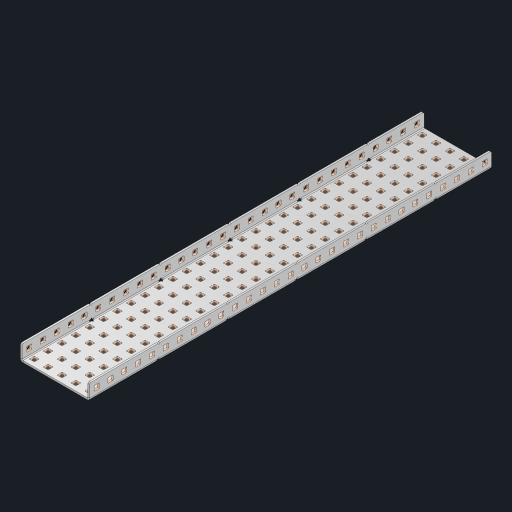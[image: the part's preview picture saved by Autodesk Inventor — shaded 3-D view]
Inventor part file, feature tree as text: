
AUTODESK INVENTOR PART (.ipt)
format: ipt  version: 2023 (Build 270158000, 158)  size: 2,219,520 bytes
history: native  units: in
note: dims shown in document units (in); Inventor stores cm internally (conversion verified against a paired STEP export)
features: other x208, extrude x202, sheet_metal_op x10, sketch x8, mirror x1, pattern_linear x1, chamfer x1
ambient origin geometry x8: Origin, YZ Plane, XZ Plane, XY Plane, X Axis, Y Axis, Z Axis, Center Point
bodies: Solid1 (feature_tree), Body (feature_tree)
feature tree (431):
  other  "Flange Pattern Plane"
  sheet_metal_op  "Flange Pattern"
  sheet_metal_op  "Body Pattern"
  other  "Arc Length"
  mirror  "Notch Mirror"
  pattern_linear  "Notch Pattern"  Spacing1=0.25in  [1 undecoded]
  chamfer  "End Chamfer"
  extrude  "Half Cut"  Depth=0.0625in
  sketch  "Sketch1"  dims[d0=2.5in]
  other  "Plate1"
  sketch  "Sketch2"  dims[d1=14.5in]
  other  "Plate2"
  sheet_metal_op  "Bend1"
  sheet_metal_op  "Corner1"
  sketch  "Sketch3"  dims[d2=0.0625in]
  other  "Flange Pattern Sketch"
  sketch  "Sketch7"  dims[d3=0.0625in]
  other  "Srf1"
  other  "Srf2"
  sketch  "Sketch8"  dims[d4=0.0312in]
  sketch  "Sketch9"  dims[d5=0.125in]
  other  "Srf91"
  sheet_metal_op  "Body Pattern Sketch"
  other  "Srf92"
  sketch  "Sketch13"  dims[d6=0.0625in]
  sketch  "Sketch14"  dims[d7=0.5in d8=90.0deg d9=0.0312in d10=0.25in d11=0.0625in d12=0.0625in d16=0.182in d17=0.02in d18=0.0625in d19=0.0in d20=0.25in d21=0.25in d46=0.172in d47=1.0in d48=0.0in d49=0.182in d50=0.02in d51=0.25in d52=0.25in d53=0.0625in d54=0.0in d55=0.172in d56=1.0in d57=0.0in d60=11.4173in d62=0.5in d63=1.9685in d65=0.5in d85=0.1473in d86=0.1782in d88=0.04in d89=0.0625in d90=0.0in d91=0.04in d92=0.0491in d95=2.5in d96=0.04in d97=0.25in d98=45.0deg d101=0.0in d102=2.497in d131=2.5in d132=11.4173in d134=0.5in d139=0.5in]
  other  "Srf856"
  other  "Srf1310"
  other  "Srf1311"
  other  "Srf1312"
  other  "Srf1376"
  other  "Srf1377"
  other  "Srf1728"
  other  "Srf1755"
  other  "Srf1878"
  other  "Srf1879"
  other  "Srf1880"
  other  "Srf1881"
  other  "Srf1882"
  other  "Srf1883"
  other  "Srf1884"
  other  "Srf1885"
  other  "Srf1886"
  other  "Srf1887"
  other  "Srf1888"
  other  "Srf1889"
  other  "Srf1890"
  other  "Srf1891"
  other  "Srf1892"
  other  "Srf1893"
  other  "Srf1894"
  other  "Srf1895"
  other  "Srf1896"
  other  "Srf1897"
  other  "Srf1898"
  other  "Srf1899"
  other  "Srf1900"
  other  "Srf1901"
  other  "Srf1902"
  other  "Srf1903"
  other  "Srf1904"
  other  "Srf1905"
  other  "Srf1906"
  other  "Srf1942"
  other  "Srf1943"
  other  "Srf1944"
  other  "Srf1945"
  other  "Srf1946"
  other  "Srf1947"
  other  "Srf1948"
  other  "Srf1949"
  other  "Srf1950"
  other  "Srf1951"
  other  "Srf1952"
  other  "Srf1953"
  other  "Srf1954"
  other  "Srf1955"
  other  "Srf1956"
  other  "Srf1957"
  other  "Srf1958"
  other  "Srf1959"
  other  "Srf1960"
  other  "Srf1961"
  other  "Srf1962"
  other  "Srf1963"
  other  "Srf1964"
  other  "Srf1965"
  other  "Srf1966"
  other  "Srf1967"
  other  "Srf1968"
  other  "Srf1969"
  other  "Srf1970"
  other  "Srf2111"
  other  "Srf2112"
  other  "Srf2113"
  other  "Srf2114"
  other  "Srf2115"
  other  "Srf2116"
  other  "Srf2117"
  other  "Srf2118"
  other  "Srf2119"
  other  "Srf2120"
  other  "Srf2121"
  other  "Srf2122"
  other  "Srf2123"
  other  "Srf2124"
  other  "Srf2125"
  other  "Srf2126"
  other  "Srf2127"
  other  "Srf2128"
  other  "Srf2129"
  other  "Srf2130"
  other  "Srf2131"
  other  "Srf2132"
  other  "Srf2133"
  other  "Srf2146"
  other  "Srf2147"
  other  "Srf2148"
  other  "Srf2149"
  other  "Srf2150"
  other  "Srf2151"
  other  "Srf2152"
  other  "Srf2153"
  other  "Srf2154"
  other  "Srf2155"
  other  "Srf2156"
  other  "Srf2157"
  other  "Srf2158"
  other  "Srf2159"
  other  "Srf2160"
  other  "Srf2161"
  other  "Srf2162"
  other  "Srf2163"
  other  "Srf2164"
  other  "Srf2165"
  other  "Srf2166"
  other  "Srf2167"
  other  "Srf2168"
  other  "Srf2169"
  other  "Srf2170"
  other  "Srf2171"
  other  "Srf2172"
  other  "Srf2173"
  other  "Srf2174"
  other  "Srf2175"
  other  "Srf2176"
  other  "Srf2177"
  other  "Srf2178"
  other  "Srf2179"
  other  "Srf2180"
  other  "Srf2181"
  other  "Srf2182"
  other  "Srf2183"
  other  "Srf2184"
  other  "Srf2185"
  other  "Srf2186"
  other  "Srf2187"
  other  "Srf2188"
  other  "Srf2189"
  other  "Srf2190"
  other  "Srf2191"
  other  "Srf2192"
  other  "Srf2193"
  other  "Srf2194"
  other  "Srf2195"
  other  "Srf2196"
  other  "Srf2197"
  other  "Srf2198"
  other  "Srf2199"
  other  "Srf2200"
  other  "Srf2201"
  other  "Srf2202"
  other  "Srf2203"
  other  "Srf2204"
  other  "Srf2205"
  other  "Srf2206"
  other  "Srf2207"
  other  "Srf2208"
  other  "Srf2209"
  other  "Srf2210"
  other  "Srf2211"
  other  "Srf2212"
  other  "Srf2213"
  other  "Srf2214"
  other  "Srf2215"
  other  "Srf2216"
  other  "Srf2217"
  other  "Srf2218"
  other  "Srf2219"
  other  "Srf2220"
  other  "Srf2221"
  other  "Srf2222"
  other  "Srf2223"
  other  "Srf2224"
  other  "Srf2225"
  other  "Srf2226"
  other  "Srf2227"
  other  "Srf2228"
  other  "Srf2229"
  other  "Srf2230"
  other  "Srf2231"
  other  "Srf2232"
  other  "Srf2233"
  other  "Srf2234"
  other  "Srf2235"
  other  "Srf2236"
  other  "Srf2237"
  other  "Srf2238"
  other  "Srf2239"
  other  "Srf2240"
  other  "Srf2241"
  other  "Srf2242"
  other  "Srf2243"
  other  "Srf2244"
  other  "Srf2245"
  other  "Srf2246"
  other  "Srf2247"
  other  "Srf2248"
  other  "Srf2249"
  other  "Srf2250"
  other  "Srf2251"
  other  "Srf2252"
  other  "Srf2253"
  other  "Srf2254"
  other  "Srf2255"
  sheet_metal_op  "Flange Stamp"
  sheet_metal_op  "Flange Circle"
  sheet_metal_op  "Body Stamp"
  sheet_metal_op  "Body Circle"
  sheet_metal_op  "Notch"
  extrude  "ExtrusionSrf2"  Depth=0.0625in
  extrude  "ExtrusionSrf92"  Depth=2.5in
  extrude  "ExtrusionSrf856"  Depth=0.02in
  extrude  "ExtrusionSrf1310"  Depth=0.0625in
  extrude  "ExtrusionSrf1311"  TaperAngle=0.0deg  [1 undecoded]
  extrude  "ExtrusionSrf1312"  Depth=0.25in
  extrude  "ExtrusionSrf1376"  Depth=0.25in
  extrude  "ExtrusionSrf1377"  Depth=2.5in
  extrude  "ExtrusionSrf1728"  Depth=2.5in TaperAngle=0.0deg
  extrude  "ExtrusionSrf1755"  Depth=2.5in
  extrude  "ExtrusionSrf1878"  Depth=0.02in
  extrude  "ExtrusionSrf1879"  Depth=0.25in
  extrude  "ExtrusionSrf1880"  Depth=0.25in
  extrude  "ExtrusionSrf1881"  Depth=0.0625in
  extrude  "ExtrusionSrf1882"  TaperAngle=0.0deg  [1 undecoded]
  extrude  "ExtrusionSrf1883"  Depth=2.5in
  extrude  "ExtrusionSrf1884"  Depth=2.5in TaperAngle=0.0deg
  extrude  "ExtrusionSrf1885"  Depth=2.5in
  extrude  "ExtrusionSrf1886"  Depth=2.5in
  extrude  "ExtrusionSrf1887"  Depth=2.5in
  extrude  "ExtrusionSrf1888"  Depth=2.5in
  extrude  "ExtrusionSrf1889"  Depth=2.5in
  extrude  "ExtrusionSrf1890"  Depth=0.0625in
  extrude  "ExtrusionSrf1891"  TaperAngle=0.0deg  [1 undecoded]
  extrude  "ExtrusionSrf1892"  Depth=2.5in
  extrude  "ExtrusionSrf1893"  Depth=2.5in
  extrude  "ExtrusionSrf1894"  Depth=2.5in
  extrude  "ExtrusionSrf1895"  Depth=0.25in TaperAngle=45.0deg
  extrude  "ExtrusionSrf1896"  TaperAngle=0.0deg  [1 undecoded]
  extrude  "ExtrusionSrf1897"  Depth=2.5in
  extrude  "ExtrusionSrf1898"  Depth=2.5in
  extrude  "ExtrusionSrf1899"  Depth=2.5in
  extrude  "ExtrusionSrf1900"  Depth=2.5in
  extrude  "ExtrusionSrf1901"  Depth=2.5in
  extrude  "ExtrusionSrf1902"  [1 undecoded]
  extrude  "ExtrusionSrf1903"  [1 undecoded]
  extrude  "ExtrusionSrf1904"  [1 undecoded]
  extrude  "ExtrusionSrf1905"  [1 undecoded]
  extrude  "ExtrusionSrf1906"  [1 undecoded]
  extrude  "ExtrusionSrf1942"  [1 undecoded]
  extrude  "ExtrusionSrf1943"  [1 undecoded]
  extrude  "ExtrusionSrf1944"  [1 undecoded]
  extrude  "ExtrusionSrf1945"  [1 undecoded]
  extrude  "ExtrusionSrf1946"  [1 undecoded]
  extrude  "ExtrusionSrf1947"  [1 undecoded]
  extrude  "ExtrusionSrf1948"  [1 undecoded]
  extrude  "ExtrusionSrf1949"  [1 undecoded]
  extrude  "ExtrusionSrf1950"  [1 undecoded]
  extrude  "ExtrusionSrf1951"  [1 undecoded]
  extrude  "ExtrusionSrf1952"  [1 undecoded]
  extrude  "ExtrusionSrf1953"  [1 undecoded]
  extrude  "ExtrusionSrf1954"  [1 undecoded]
  extrude  "ExtrusionSrf1955"  [1 undecoded]
  extrude  "ExtrusionSrf1956"  [1 undecoded]
  extrude  "ExtrusionSrf1957"  [1 undecoded]
  extrude  "ExtrusionSrf1958"  [1 undecoded]
  extrude  "ExtrusionSrf1959"  [1 undecoded]
  extrude  "ExtrusionSrf1960"  [1 undecoded]
  extrude  "ExtrusionSrf1961"  [1 undecoded]
  extrude  "ExtrusionSrf1962"  [1 undecoded]
  extrude  "ExtrusionSrf1963"  [1 undecoded]
  extrude  "ExtrusionSrf1964"  [1 undecoded]
  extrude  "ExtrusionSrf1965"  [1 undecoded]
  extrude  "ExtrusionSrf1966"  [1 undecoded]
  extrude  "ExtrusionSrf1967"  [1 undecoded]
  extrude  "ExtrusionSrf1968"  [1 undecoded]
  extrude  "ExtrusionSrf1969"  [1 undecoded]
  extrude  "ExtrusionSrf1970"  [1 undecoded]
  extrude  "ExtrusionSrf2111"  [1 undecoded]
  extrude  "ExtrusionSrf2112"  [1 undecoded]
  extrude  "ExtrusionSrf2113"  [1 undecoded]
  extrude  "ExtrusionSrf2114"  [1 undecoded]
  extrude  "ExtrusionSrf2115"  [1 undecoded]
  extrude  "ExtrusionSrf2116"  [1 undecoded]
  extrude  "ExtrusionSrf2117"  [1 undecoded]
  extrude  "ExtrusionSrf2118"  [1 undecoded]
  extrude  "ExtrusionSrf2119"  [1 undecoded]
  extrude  "ExtrusionSrf2120"  [1 undecoded]
  extrude  "ExtrusionSrf2121"  [1 undecoded]
  extrude  "ExtrusionSrf2122"  [1 undecoded]
  extrude  "ExtrusionSrf2123"  [1 undecoded]
  extrude  "ExtrusionSrf2124"  [1 undecoded]
  extrude  "ExtrusionSrf2125"  [1 undecoded]
  extrude  "ExtrusionSrf2126"  [1 undecoded]
  extrude  "ExtrusionSrf2127"  [1 undecoded]
  extrude  "ExtrusionSrf2128"  [1 undecoded]
  extrude  "ExtrusionSrf2129"  [1 undecoded]
  extrude  "ExtrusionSrf2130"  [1 undecoded]
  extrude  "ExtrusionSrf2131"  [1 undecoded]
  extrude  "ExtrusionSrf2132"  [1 undecoded]
  extrude  "ExtrusionSrf2133"  [1 undecoded]
  extrude  "ExtrusionSrf2146"  [1 undecoded]
  extrude  "ExtrusionSrf2147"  [1 undecoded]
  extrude  "ExtrusionSrf2148"  [1 undecoded]
  extrude  "ExtrusionSrf2149"  [1 undecoded]
  extrude  "ExtrusionSrf2150"  [1 undecoded]
  extrude  "ExtrusionSrf2151"  [1 undecoded]
  extrude  "ExtrusionSrf2152"  [1 undecoded]
  extrude  "ExtrusionSrf2153"  [1 undecoded]
  extrude  "ExtrusionSrf2154"  [1 undecoded]
  extrude  "ExtrusionSrf2155"  [1 undecoded]
  extrude  "ExtrusionSrf2156"  [1 undecoded]
  extrude  "ExtrusionSrf2157"  [1 undecoded]
  extrude  "ExtrusionSrf2158"  [1 undecoded]
  extrude  "ExtrusionSrf2159"  [1 undecoded]
  extrude  "ExtrusionSrf2160"  [1 undecoded]
  extrude  "ExtrusionSrf2161"  [1 undecoded]
  extrude  "ExtrusionSrf2162"  [1 undecoded]
  extrude  "ExtrusionSrf2163"  [1 undecoded]
  extrude  "ExtrusionSrf2164"  [1 undecoded]
  extrude  "ExtrusionSrf2165"  [1 undecoded]
  extrude  "ExtrusionSrf2166"  [1 undecoded]
  extrude  "ExtrusionSrf2167"  [1 undecoded]
  extrude  "ExtrusionSrf2168"  [1 undecoded]
  extrude  "ExtrusionSrf2169"  [1 undecoded]
  extrude  "ExtrusionSrf2170"  [1 undecoded]
  extrude  "ExtrusionSrf2171"  [1 undecoded]
  extrude  "ExtrusionSrf2172"  [1 undecoded]
  extrude  "ExtrusionSrf2173"  [1 undecoded]
  extrude  "ExtrusionSrf2174"  [1 undecoded]
  extrude  "ExtrusionSrf2175"  [1 undecoded]
  extrude  "ExtrusionSrf2176"  [1 undecoded]
  extrude  "ExtrusionSrf2177"  [1 undecoded]
  extrude  "ExtrusionSrf2178"  [1 undecoded]
  extrude  "ExtrusionSrf2179"  [1 undecoded]
  extrude  "ExtrusionSrf2180"  [1 undecoded]
  extrude  "ExtrusionSrf2181"  [1 undecoded]
  extrude  "ExtrusionSrf2182"  [1 undecoded]
  extrude  "ExtrusionSrf2183"  [1 undecoded]
  extrude  "ExtrusionSrf2184"  [1 undecoded]
  extrude  "ExtrusionSrf2185"  [1 undecoded]
  extrude  "ExtrusionSrf2186"  [1 undecoded]
  extrude  "ExtrusionSrf2187"  [1 undecoded]
  extrude  "ExtrusionSrf2188"  [1 undecoded]
  extrude  "ExtrusionSrf2189"  [1 undecoded]
  extrude  "ExtrusionSrf2190"  [1 undecoded]
  extrude  "ExtrusionSrf2191"  [1 undecoded]
  extrude  "ExtrusionSrf2192"  [1 undecoded]
  extrude  "ExtrusionSrf2193"  [1 undecoded]
  extrude  "ExtrusionSrf2194"  [1 undecoded]
  extrude  "ExtrusionSrf2195"  [1 undecoded]
  extrude  "ExtrusionSrf2196"  [1 undecoded]
  extrude  "ExtrusionSrf2197"  [1 undecoded]
  extrude  "ExtrusionSrf2198"  [1 undecoded]
  extrude  "ExtrusionSrf2199"  [1 undecoded]
  extrude  "ExtrusionSrf2200"  [1 undecoded]
  extrude  "ExtrusionSrf2201"  [1 undecoded]
  extrude  "ExtrusionSrf2202"  [1 undecoded]
  extrude  "ExtrusionSrf2203"  [1 undecoded]
  extrude  "ExtrusionSrf2204"  [1 undecoded]
  extrude  "ExtrusionSrf2205"  [1 undecoded]
  extrude  "ExtrusionSrf2206"  [1 undecoded]
  extrude  "ExtrusionSrf2207"  [1 undecoded]
  extrude  "ExtrusionSrf2208"  [1 undecoded]
  extrude  "ExtrusionSrf2209"  [1 undecoded]
  extrude  "ExtrusionSrf2210"  [1 undecoded]
  extrude  "ExtrusionSrf2211"  [1 undecoded]
  extrude  "ExtrusionSrf2212"  [1 undecoded]
  extrude  "ExtrusionSrf2213"  [1 undecoded]
  extrude  "ExtrusionSrf2214"  [1 undecoded]
  extrude  "ExtrusionSrf2215"  [1 undecoded]
  extrude  "ExtrusionSrf2216"  [1 undecoded]
  extrude  "ExtrusionSrf2217"  [1 undecoded]
  extrude  "ExtrusionSrf2218"  [1 undecoded]
  extrude  "ExtrusionSrf2219"  [1 undecoded]
  extrude  "ExtrusionSrf2220"  [1 undecoded]
  extrude  "ExtrusionSrf2221"  [1 undecoded]
  extrude  "ExtrusionSrf2222"  [1 undecoded]
  extrude  "ExtrusionSrf2223"  [1 undecoded]
  extrude  "ExtrusionSrf2224"  [1 undecoded]
  extrude  "ExtrusionSrf2225"  [1 undecoded]
  extrude  "ExtrusionSrf2226"  [1 undecoded]
  extrude  "ExtrusionSrf2227"  [1 undecoded]
  extrude  "ExtrusionSrf2228"  [1 undecoded]
  extrude  "ExtrusionSrf2229"  [1 undecoded]
  extrude  "ExtrusionSrf2230"  [1 undecoded]
  extrude  "ExtrusionSrf2231"  [1 undecoded]
  extrude  "ExtrusionSrf2232"  [1 undecoded]
  extrude  "ExtrusionSrf2233"  [1 undecoded]
  extrude  "ExtrusionSrf2234"  [1 undecoded]
  extrude  "ExtrusionSrf2235"  [1 undecoded]
  extrude  "ExtrusionSrf2236"  [1 undecoded]
  extrude  "ExtrusionSrf2237"  [1 undecoded]
  extrude  "ExtrusionSrf2238"  [1 undecoded]
  extrude  "ExtrusionSrf2239"  [1 undecoded]
  extrude  "ExtrusionSrf2240"  [1 undecoded]
  extrude  "ExtrusionSrf2241"  [1 undecoded]
  extrude  "ExtrusionSrf2242"  [1 undecoded]
  extrude  "ExtrusionSrf2243"  [1 undecoded]
  extrude  "ExtrusionSrf2244"  [1 undecoded]
  extrude  "ExtrusionSrf2245"  [1 undecoded]
  extrude  "ExtrusionSrf2246"  [1 undecoded]
  extrude  "ExtrusionSrf2247"  [1 undecoded]
  extrude  "ExtrusionSrf2248"  [1 undecoded]
  extrude  "ExtrusionSrf2249"  [1 undecoded]
  extrude  "ExtrusionSrf2250"  [1 undecoded]
  extrude  "ExtrusionSrf2251"  [1 undecoded]
  extrude  "ExtrusionSrf2252"  [1 undecoded]
  extrude  "ExtrusionSrf2253"  [1 undecoded]
  extrude  "ExtrusionSrf2254"  [1 undecoded]
  extrude  "ExtrusionSrf2255"  [1 undecoded]
note: 172 required parameter values undecoded (feature->parameter linkage not recoverable at this tier; creation-order binding heuristic only, values carry confidence <= 0.55)
